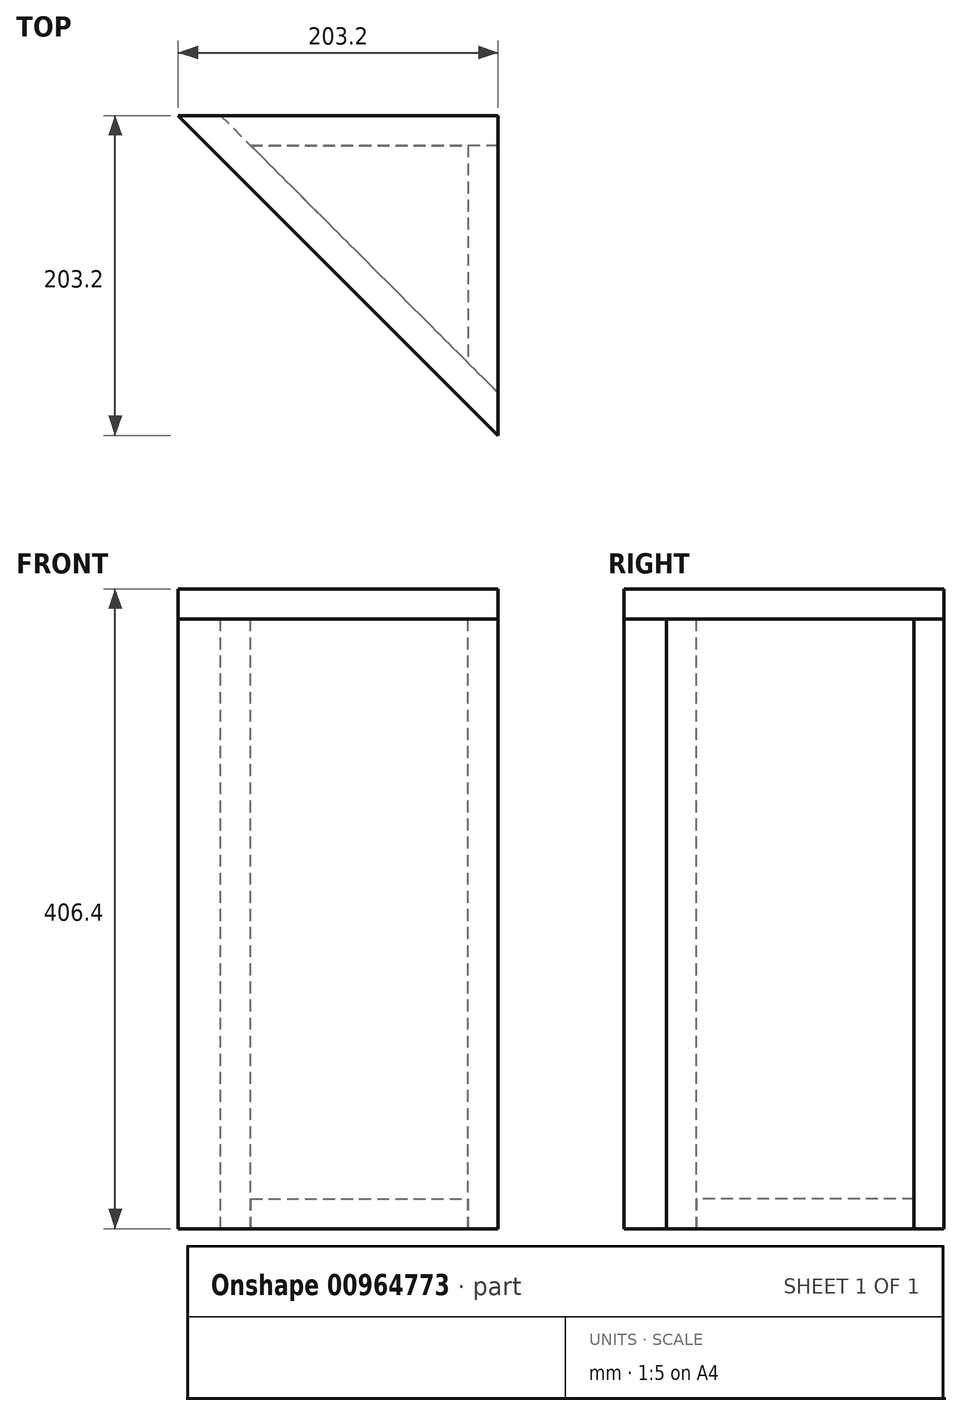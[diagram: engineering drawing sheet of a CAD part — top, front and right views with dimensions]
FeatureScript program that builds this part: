
annotation { "Feature Type Name" : "Feature", "Feature Type Description" : "" }
export const myFeature = defineFeature(function(context is Context, id is Id, definition is map)
    precondition{}
    {
        {
            var Q0;
            Q0=qCreatedBy(makeId("Top.planeOp"),FACE);
            var sketch = newSketch(context, id + "F0", { "sketchPlane" : qUnion([Q0])});
            skLineSegment(sketch, "E0.bottom", {"start": v(101.6, 101.6) * mm, "end": v(-101.6, 101.6) * mm});
            skLineSegment(sketch, "E0.top", {"start": v(101.6, -101.6) * mm, "end": v(-101.6, -101.6) * mm});
            skLineSegment(sketch, "E0.left", {"start": v(101.6, 101.6) * mm, "end": v(101.6, -101.6) * mm});
            skLineSegment(sketch, "E0.right", {"start": v(-101.6, 101.6) * mm, "end": v(-101.6, -101.6) * mm});
            skPoint(sketch, "E0.middle", {"position": v(0, 0) * mm});
            skLineSegment(sketch, "E1", {"start": v(-101.6, 101.6) * mm, "end": v(101.6, -101.6) * mm});
            skLineSegment(sketch, "E2", {"start": v(-74.66, 101.6) * mm, "end": v(101.6, -74.66) * mm});
            skLineSegment(sketch, "E3", {"start": v(101.6, 82.55) * mm, "end": v(-55.6, 82.55) * mm});
            skLineSegment(sketch, "E4", {"start": v(82.55, 82.55) * mm, "end": v(82.55, -55.6) * mm});
            skSolve(sketch);
        }
        {
            var Q0;
            {var subQ4=sQuery(id+"F0.wireOp",EDGE,"E1");Q0=makeQuery(id+"F0.imprint","IMPRINT",FACE,{"disambiguationData":[TD([[makeQuery(id+"F0.imprint","IMPRINT",EDGE,{"derivedFrom":subQ4}),1.0]])]});}
            extrude(context, id + "F1", {"entities" : qUnion([Q0]), "oppositeDirection" : true, "depth" : 387.35 * mm, "offsetDistance" : 25.4 * mm});
        }
        {
            var Q0;
            {var subQ1=sQuery(id+"F0.wireOp",EDGE,"E0.left");var subQ4=sQuery(id+"F0.wireOp",EDGE,"E0.bottom");var subQ5=makeQuery(id+"F0.imprint","INTERSECT",VERTEX,{"derivedFrom":[subQ4,subQ1]});Q0=makeQuery(id+"F0.imprint","IMPRINT",FACE,{"disambiguationData":[TD([[makeQuery(id+"F0.imprint","IMPRINT",EDGE,{"disambiguationData":[TD([[subQ5,-1.0]])],"derivedFrom":subQ4}),1.0]])]});}
            extrude(context, id + "F2", {"entities" : qUnion([Q0]), "oppositeDirection" : true, "depth" : 387.35 * mm, "offsetDistance" : 25.4 * mm});
        }
        {
            var Q0;
            {var subQ5=sQuery(id+"F0.wireOp",EDGE,"E4");Q0=makeQuery(id+"F0.imprint","IMPRINT",FACE,{"disambiguationData":[TD([[makeQuery(id+"F0.imprint","IMPRINT",EDGE,{"derivedFrom":subQ5}),1.0]])]});}
            extrude(context, id + "F3", {"entities" : qUnion([Q0]), "oppositeDirection" : true, "depth" : 387.35 * mm, "offsetDistance" : 25.4 * mm});
        }
        {
            var Q0;
            {var subQ1=sQuery(id+"F0.wireOp",EDGE,"E0.left");var subQ4=sQuery(id+"F0.wireOp",EDGE,"E0.bottom");var subQ5=makeQuery(id+"F0.imprint","INTERSECT",VERTEX,{"derivedFrom":[subQ4,subQ1]});Q0=makeQuery(id+"F0.imprint","IMPRINT",FACE,{"disambiguationData":[TD([[makeQuery(id+"F0.imprint","IMPRINT",EDGE,{"disambiguationData":[TD([[subQ5,-1.0]])],"derivedFrom":subQ4}),1.0]])]});}
            var Q1;
            {var subQ4=sQuery(id+"F0.wireOp",EDGE,"E1");Q1=makeQuery(id+"F0.imprint","IMPRINT",FACE,{"disambiguationData":[TD([[makeQuery(id+"F0.imprint","IMPRINT",EDGE,{"derivedFrom":subQ4}),1.0]])]});}
            var Q2;
            {var subQ3=sQuery(id+"F0.wireOp",EDGE,"E4");Q2=makeQuery(id+"F0.imprint","IMPRINT",FACE,{"disambiguationData":[TD([[makeQuery(id+"F0.imprint","IMPRINT",EDGE,{"derivedFrom":subQ3}),-1.0]])]});}
            var Q3;
            {var subQ5=sQuery(id+"F0.wireOp",EDGE,"E4");Q3=makeQuery(id+"F0.imprint","IMPRINT",FACE,{"disambiguationData":[TD([[makeQuery(id+"F0.imprint","IMPRINT",EDGE,{"derivedFrom":subQ5}),1.0]])]});}
            extrude(context, id + "F4", {"entities" : qUnion([Q0, Q1, Q2, Q3]), "depth" : 19.05 * mm, "offsetDistance" : 25.4 * mm});
        }
        {
            var Q0;
            Q0=makeQuery(id+"F1.opExtrude","CAP_FACE",FACE,{"disambiguationData":[OSD([sQuery(id+"F0.wireOp",EDGE,"E0.bottom"),sQuery(id+"F0.wireOp",EDGE,"E0.left"),sQuery(id+"F0.wireOp",EDGE,"E1"),sQuery(id+"F0.wireOp",EDGE,"E2")])],"isStart":false});
            var sketch = newSketch(context, id + "F5", { "sketchPlane" : qUnion([Q0])});
            skLineSegment(sketch, "E5", {"start": v(82.55, 55.6) * mm, "end": v(-55.6, -82.55) * mm});
            skLineSegment(sketch, "E6", {"start": v(-55.6, -82.55) * mm, "end": v(82.55, -82.55) * mm});
            skLineSegment(sketch, "E7", {"start": v(82.55, -82.55) * mm, "end": v(82.55, 55.6) * mm});
            skSolve(sketch);
        }
        {
            var Q0;
            Q0=makeQuery(id+"F5.imprint","IMPRINT",FACE,{"disambiguationData":[TD([[makeQuery(id+"F5.imprint","IMPRINT",EDGE,{"derivedFrom":sQuery(id+"F5.wireOp",EDGE,"E5")}),-1.0]])]});
            extrude(context, id + "F6", {"entities" : qUnion([Q0]), "oppositeDirection" : true, "depth" : 19.05 * mm, "offsetDistance" : 25.4 * mm});
        }
    });
